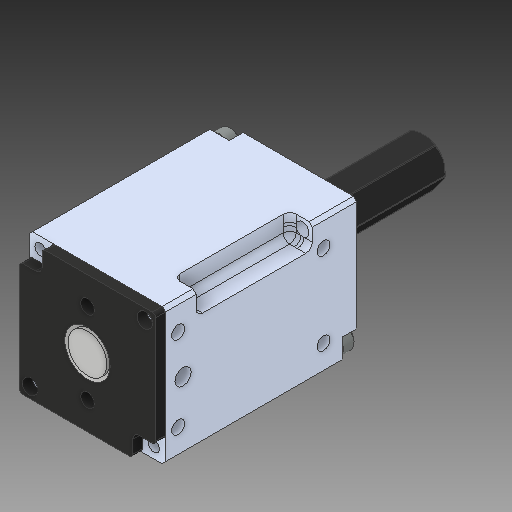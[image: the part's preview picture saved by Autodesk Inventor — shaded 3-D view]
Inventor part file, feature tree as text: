
AUTODESK INVENTOR PART (.ipt)
format: ipt  version: 2019 (Build 230136000, 136)  size: 4,282,368 bytes
history: native  units: in
note: dims shown in document units (in); Inventor stores cm internally (conversion verified against a paired STEP export)
features: extrude x1, sketch x1
ambient origin geometry x8: Origin, YZ Plane, XZ Plane, XY Plane, X Axis, Y Axis, Z Axis, Center Point
bodies: Solid2 (feature_tree), Solid1 (feature_tree)
feature tree (2):
  extrude  "Extrusion1"  [1 undecoded]
  sketch  "Sketch1"  dims[d0=0.3937in d1=0.0in]
note: 1 required parameter value undecoded (feature->parameter linkage not recoverable at this tier; creation-order binding heuristic only, values carry confidence <= 0.55)
